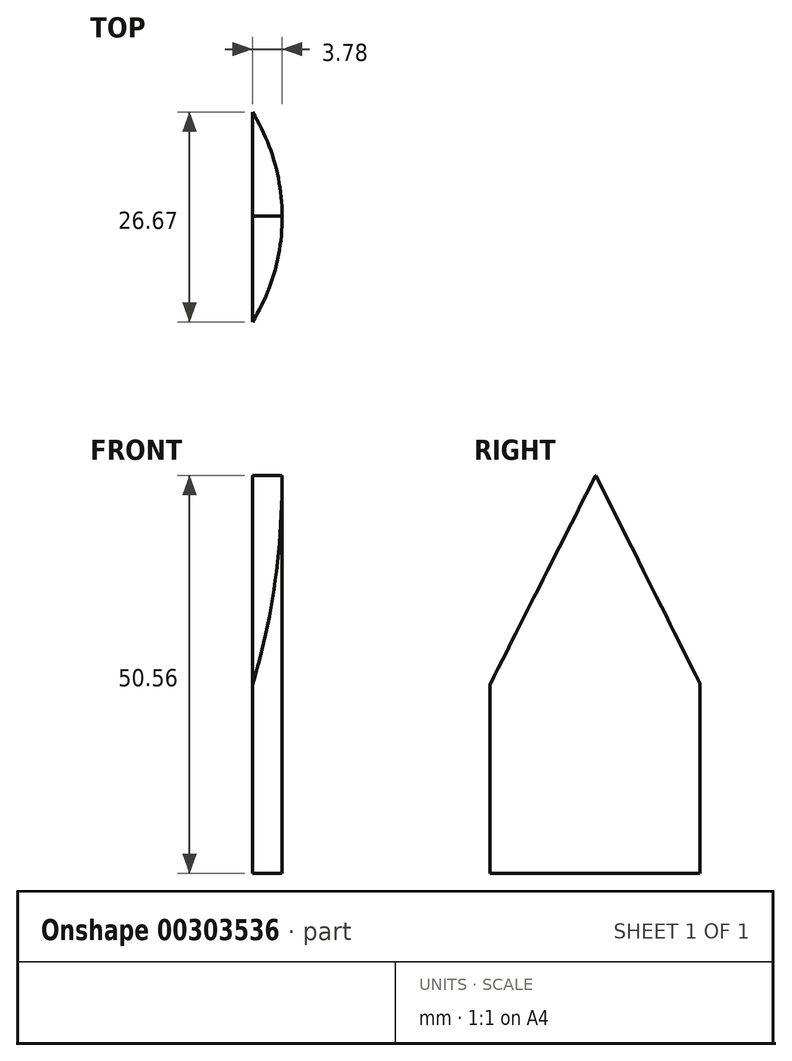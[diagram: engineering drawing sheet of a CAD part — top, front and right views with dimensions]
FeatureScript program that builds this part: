
annotation { "Feature Type Name" : "Feature", "Feature Type Description" : "" }
export const myFeature = defineFeature(function(context is Context, id is Id, definition is map)
    precondition{}
    {
        {
            var Q0;
            Q0=qCreatedBy(makeId("Top.planeOp"),FACE);
            var sketch = newSketch(context, id + "F0", { "sketchPlane" : qUnion([Q0])});
            skCircle(sketch, "E0", {"center": v(-21.62, 16.48) * mm, "radius": 25.4 * mm});
            skSolve(sketch);
        }
        {
            var Q0;
            Q0 = qSketchRegion(id + "F0", true);
            extrude(context, id + "F1", {"entities" : qUnion([Q0]), "depth" : 50.8 * mm});
        }
        {
            var Q0;
            Q0=qCreatedBy(makeId("Right.planeOp"),FACE);
            var sketch = newSketch(context, id + "F2", { "sketchPlane" : qUnion([Q0])});
            skLineSegment(sketch, "E1", {"start": v(-8.97, 0.24) * mm, "end": v(16.6, 50.83) * mm});
            skLineSegment(sketch, "E2", {"start": v(16.6, 50.83) * mm, "end": v(41.89, 0.24) * mm});
            skPoint(sketch, "E3.startSnap0", {"position": v(29.24, 51.5) * mm});
            skPoint(sketch, "E3.start.orphan", {"position": v(-9.51, 51.5) * mm});
            skPoint(sketch, "E4.end.orphan", {"position": v(41.89, 52.18) * mm});
            skLineSegment(sketch, "E5", {"start": v(-8.97, 0.24) * mm, "end": v(41.89, 0.24) * mm});
            skSolve(sketch);
        }
        {
            var Q0;
            Q0 = qSketchRegion(id + "F2", true);
            extrude(context, id + "F3", {"entities" : qUnion([Q0]), "operationType" : NewBodyOperationType.INTERSECT, "depth" : 25.4 * mm});
        }
    });
